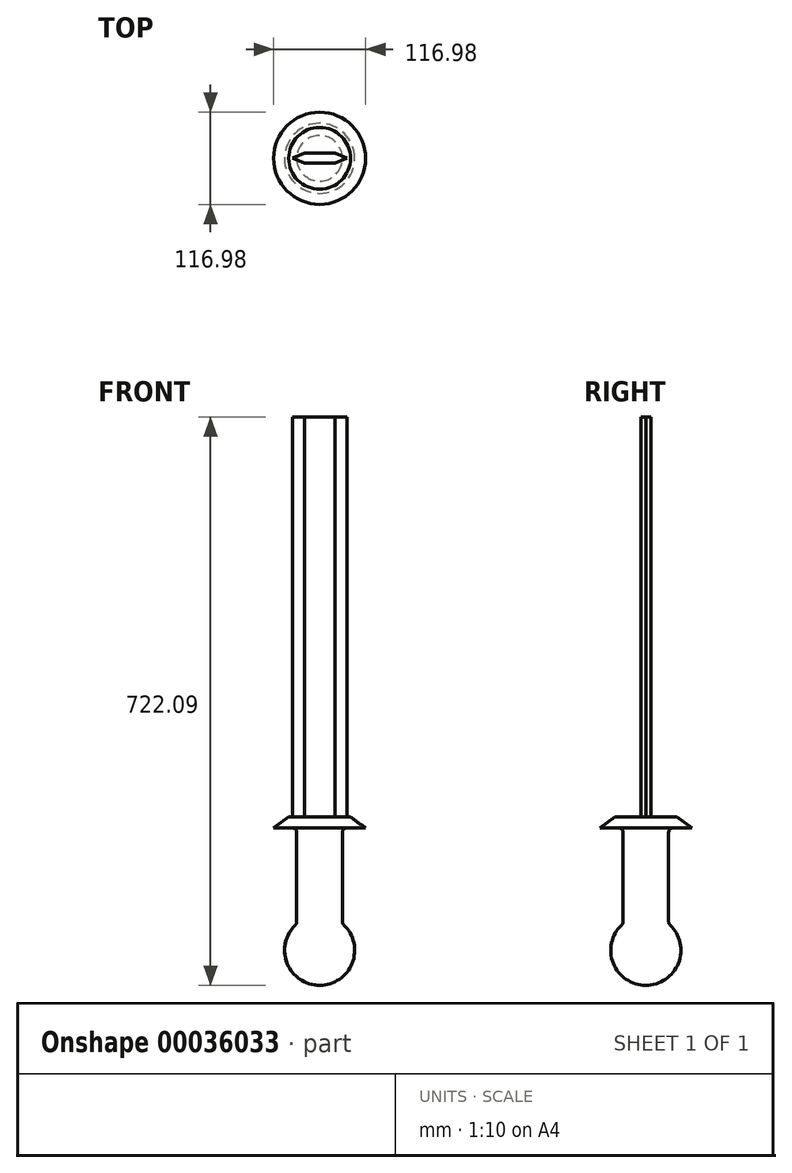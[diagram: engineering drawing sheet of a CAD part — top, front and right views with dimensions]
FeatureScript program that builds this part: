
annotation { "Feature Type Name" : "Feature", "Feature Type Description" : "" }
export const myFeature = defineFeature(function(context is Context, id is Id, definition is map)
    precondition{}
    {
        {
            var Q0;
            Q0=qCreatedBy(makeId("Front.planeOp"),FACE);
            var sketch = newSketch(context, id + "F0", { "sketchPlane" : qUnion([Q0])});
            skLineSegment(sketch, "E0.left", {"start": v(-22.49, 129.5) * mm, "end": v(-22.49, 8.12) * mm});
            skLineSegment(sketch, "E0.right", {"start": v(6.55, 129.5) * mm, "end": v(6.55, -25.65) * mm});
            skArc(sketch, "E1", {"start": v(-22.49, 8.12) * mm, "mid": v(-35.2, -41.13) * mm, "end": v(6.55, -70.19) * mm});
            skLineSegment(sketch, "E2", {"start": v(6.55, -25.65) * mm, "end": v(6.55, -70.19) * mm});
            skLineSegment(sketch, "E3.bottom", {"start": v(-22.49, 129.5) * mm, "end": v(-32.68, 129.5) * mm});
            skLineSegment(sketch, "E3.top", {"start": v(6.55, 143.9) * mm, "end": v(-32.68, 143.9) * mm});
            skLineSegment(sketch, "E3.left", {"start": v(6.55, 129.5) * mm, "end": v(6.55, 143.9) * mm});
            skLineSegment(sketch, "E4", {"start": v(-32.68, 129.5) * mm, "end": v(-51.94, 129.5) * mm});
            skLineSegment(sketch, "E5", {"start": v(-51.94, 129.5) * mm, "end": v(-32.68, 143.9) * mm});
            skSolve(sketch);
        }
        {
            var Q0;
            Q0=makeQuery(id+"F0.imprint","IMPRINT",FACE,{"disambiguationData":[TD([[makeQuery(id+"F0.imprint","IMPRINT",EDGE,{"derivedFrom":sQuery(id+"F0.wireOp",EDGE,"E0.left")}),1.0]])]});
            var Q1;
            Q1=sQuery(id+"F0.wireOp",EDGE,"E0.right");
            revolve(context, id + "F1", {"entities" : qUnion([Q0]), "axis" : qUnion([Q1]), "revolveType" : RevolveType.FULL});
        }
        {
            var Q0;
            Q0=makeQuery(id+"F1.opRevolve","SWEPT_FACE",FACE,{"disambiguationData":[OSD([sQuery(id+"F0.wireOp",EDGE,"E3.top")])]});
            var sketch = newSketch(context, id + "F2", { "sketchPlane" : qUnion([Q0])});
            skLineSegment(sketch, "E6.rect.bottom", {"start": v(25.87, 6.35) * mm, "end": v(-12.77, 6.35) * mm});
            skLineSegment(sketch, "E6.rect.top", {"start": v(25.87, -6.35) * mm, "end": v(-12.77, -6.35) * mm});
            skLineSegment(sketch, "E6.rect.left", {"start": v(25.87, 6.35) * mm, "end": v(25.87, -6.35) * mm});
            skLineSegment(sketch, "E6.rect.right", {"start": v(-12.77, 6.35) * mm, "end": v(-12.77, -6.35) * mm});
            skPoint(sketch, "E6.rect.middle", {"position": v(6.55, 0) * mm});
            skLineSegment(sketch, "E7", {"start": v(-12.77, 0) * mm, "end": v(-28, 0) * mm});
            skPoint(sketch, "E7.endSnap0", {"position": v(-12.77, 0) * mm});
            skLineSegment(sketch, "E8", {"start": v(-28, 0) * mm, "end": v(-12.77, 6.35) * mm});
            skLineSegment(sketch, "E9", {"start": v(-28, 0) * mm, "end": v(-12.77, -6.35) * mm});
            skLineSegment(sketch, "E10", {"start": v(25.87, 0) * mm, "end": v(41.1, 0) * mm});
            skLineSegment(sketch, "E11", {"start": v(41.1, 0) * mm, "end": v(25.87, -6.35) * mm});
            skLineSegment(sketch, "E12", {"start": v(25.87, 6.35) * mm, "end": v(41.1, 0) * mm});
            skSolve(sketch);
        }
        {
            var Q0;
            {var subQ1=sQuery(id+"F2.wireOp",EDGE,"E7");Q0=makeQuery(id+"F2.imprint","IMPRINT",FACE,{"disambiguationData":[TD([[makeQuery(id+"F2.imprint","IMPRINT",EDGE,{"derivedFrom":subQ1}),1.0]])]});}
            var Q1;
            {var subQ1=sQuery(id+"F2.wireOp",EDGE,"E7");Q1=makeQuery(id+"F2.imprint","IMPRINT",FACE,{"disambiguationData":[TD([[makeQuery(id+"F2.imprint","IMPRINT",EDGE,{"derivedFrom":subQ1}),-1.0]])]});}
            var Q2;
            {var subQ1=sQuery(id+"F2.wireOp",EDGE,"E10");Q2=makeQuery(id+"F2.imprint","IMPRINT",FACE,{"disambiguationData":[TD([[makeQuery(id+"F2.imprint","IMPRINT",EDGE,{"derivedFrom":subQ1}),-1.0]])]});}
            var Q3;
            {var subQ1=sQuery(id+"F2.wireOp",EDGE,"E10");Q3=makeQuery(id+"F2.imprint","IMPRINT",FACE,{"disambiguationData":[TD([[makeQuery(id+"F2.imprint","IMPRINT",EDGE,{"derivedFrom":subQ1}),1.0]])]});}
            var Q4;
            {var subQ3=sQuery(id+"F2.wireOp",EDGE,"E6.rect.bottom");Q4=makeQuery(id+"F2.imprint","IMPRINT",FACE,{"disambiguationData":[TD([[makeQuery(id+"F2.imprint","IMPRINT",EDGE,{"derivedFrom":subQ3}),1.0]])]});}
            extrude(context, id + "F3", {"entities" : qUnion([Q0, Q1, Q2, Q3, Q4]), "operationType" : NewBodyOperationType.ADD, "depth" : 508 * mm});
        }
        {
            var Q0;
            Q0=makeQuery(id+"F1.opRevolve","SWEPT_EDGE",EDGE,{"disambiguationData":[OSD([sQuery(id+"F0.wireOp",EDGE,"E0.left"),sQuery(id+"F0.wireOp",EDGE,"E3.bottom")])]});
            var Q1;
            Q1=makeQuery(id+"F1.opRevolve","SWEPT_EDGE",EDGE,{"disambiguationData":[OSD([sQuery(id+"F0.wireOp",EDGE,"E0.left"),sQuery(id+"F0.wireOp",EDGE,"E1")])]});
            fillet(context, id + "F4", {"entities" : qUnion([Q0, Q1]), "radius" : 5.08 * mm, "tangentPropagation" : true, "allowEdgeOverflow" : false});
        }
    });
